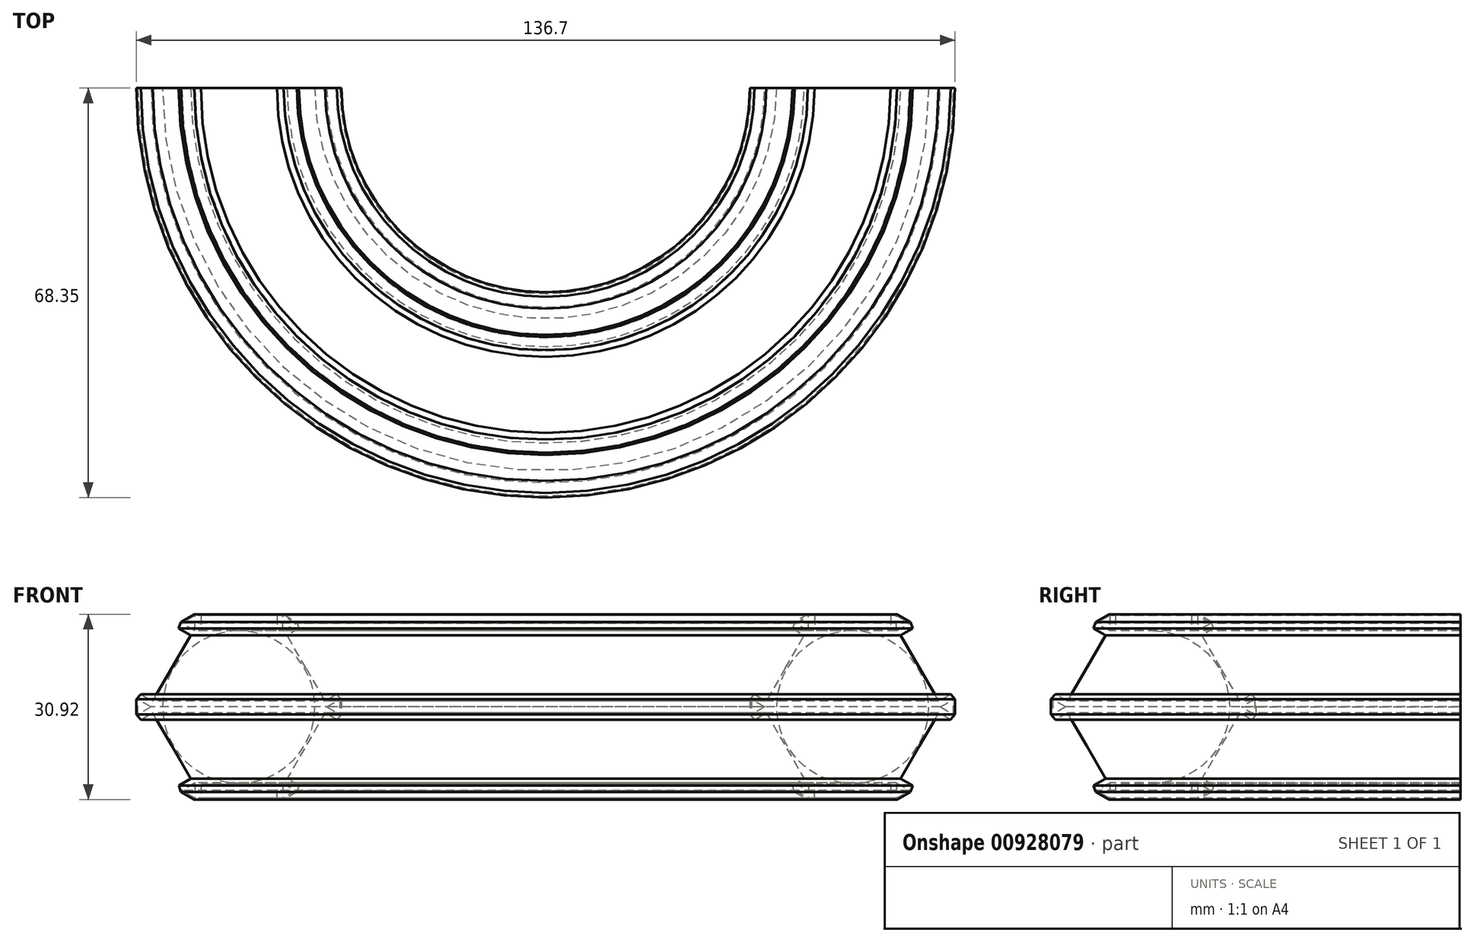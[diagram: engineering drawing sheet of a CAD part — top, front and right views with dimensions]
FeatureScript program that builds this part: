
annotation { "Feature Type Name" : "Feature", "Feature Type Description" : "" }
export const myFeature = defineFeature(function(context is Context, id is Id, definition is map)
    precondition{}
    {
        {
            var Q0;
            Q0=qCreatedBy(makeId("Top.planeOp"),FACE);
            var sketch = newSketch(context, id + "F0", { "sketchPlane" : qUnion([Q0])});
            skLineSegment(sketch, "E0", {"start": v(0, 0) * mm, "end": v(-50.8, 0) * mm});
            skCircle(sketch, "E1", {"center": v(0, 0) * mm, "radius": 50.8 * mm});
            skSolve(sketch);
        }
        {
            var Q0;
            Q0=qCreatedBy(makeId("Front.planeOp"),FACE);
            var sketch = newSketch(context, id + "F1", { "sketchPlane" : qUnion([Q0])});
            skCircle(sketch, "E2", {"center": v(-51.22, 0) * mm, "radius": 12.7 * mm});
            skPoint(sketch, "E3.0.midPoint", {"position": v(-51.22, 12.7) * mm});
            skLineSegment(sketch, "E4", {"start": v(-65.88, 0) * mm, "end": v(-68.08, -1.27) * mm});
            skLineSegment(sketch, "E5", {"start": v(-58.55, -12.7) * mm, "end": v(-60.75, -13.97) * mm});
            skLineSegment(sketch, "E6", {"start": v(-58.55, -12.7) * mm, "end": v(-58.55, -15.23) * mm});
            skLineSegment(sketch, "E7", {"start": v(-43.88, -12.7) * mm, "end": v(-43.88, -15.23) * mm});
            skLineSegment(sketch, "E8", {"start": v(-43.88, -12.7) * mm, "end": v(-41.67, -13.98) * mm});
            skLineSegment(sketch, "E9", {"start": v(-36.55, 0) * mm, "end": v(-34.36, -1.26) * mm});
            skLineSegment(sketch, "E10", {"start": v(-36.55, 0) * mm, "end": v(-34.36, 1.26) * mm});
            skLineSegment(sketch, "E11", {"start": v(-43.88, 12.7) * mm, "end": v(-41.7, 13.97) * mm});
            skLineSegment(sketch, "E12", {"start": v(-58.55, 12.7) * mm, "end": v(-58.55, 15.25) * mm});
            skLineSegment(sketch, "E13", {"start": v(-43.88, 12.7) * mm, "end": v(-43.88, 15.25) * mm});
            skLineSegment(sketch, "E14", {"start": v(-58.55, 12.7) * mm, "end": v(-60.76, 13.98) * mm});
            skLineSegment(sketch, "E15", {"start": v(-65.88, 0) * mm, "end": v(-68.08, 1.27) * mm});
            skLineSegment(sketch, "E16", {"start": v(-51.22, 12.96) * mm, "end": v(-57.56, 12.96) * mm});
            skLineSegment(sketch, "E17", {"start": v(-51.22, 12.96) * mm, "end": v(-44.86, 12.96) * mm});
            skLineSegment(sketch, "E18", {"start": v(-62.43, 6.47) * mm, "end": v(-59.25, 11.97) * mm});
            skLineSegment(sketch, "E19", {"start": v(-62.43, -6.47) * mm, "end": v(-65.6, -0.98) * mm});
            skLineSegment(sketch, "E20", {"start": v(-62.43, -6.47) * mm, "end": v(-59.26, -11.97) * mm});
            skLineSegment(sketch, "E21", {"start": v(-51.22, -12.95) * mm, "end": v(-57.56, -12.95) * mm});
            skLineSegment(sketch, "E22", {"start": v(-51.22, -12.95) * mm, "end": v(-44.86, -12.95) * mm});
            skLineSegment(sketch, "E23", {"start": v(-40, -6.48) * mm, "end": v(-36.83, -0.97) * mm});
            skLineSegment(sketch, "E24", {"start": v(-40, -6.48) * mm, "end": v(-43.16, -11.98) * mm});
            skLineSegment(sketch, "E25", {"start": v(-40, 6.48) * mm, "end": v(-43.17, 11.98) * mm});
            skLineSegment(sketch, "E26", {"start": v(-40, 6.48) * mm, "end": v(-36.83, 1) * mm});
            skLineSegment(sketch, "E27", {"start": v(-62.43, 6.47) * mm, "end": v(-65.6, 0.96) * mm});
            skLineSegment(sketch, "E28", {"start": v(-61.25, 13.12) * mm, "end": v(-59.25, 11.97) * mm});
            skLineSegment(sketch, "E29", {"start": v(-57.56, 15.25) * mm, "end": v(-57.56, 12.96) * mm});
            skLineSegment(sketch, "E30", {"start": v(-67.6, -2.12) * mm, "end": v(-65.6, -0.98) * mm});
            skLineSegment(sketch, "E31", {"start": v(-44.86, -15.23) * mm, "end": v(-44.86, -12.95) * mm});
            skLineSegment(sketch, "E32", {"start": v(-57.56, -12.95) * mm, "end": v(-57.56, -15.23) * mm});
            skLineSegment(sketch, "E33", {"start": v(-41.18, -13.12) * mm, "end": v(-43.16, -11.98) * mm});
            skLineSegment(sketch, "E34", {"start": v(-34.85, -2.11) * mm, "end": v(-36.83, -0.97) * mm});
            skLineSegment(sketch, "E35", {"start": v(-34.86, 2.13) * mm, "end": v(-36.83, 1) * mm});
            skLineSegment(sketch, "E36", {"start": v(-41.2, 13.11) * mm, "end": v(-43.17, 11.98) * mm});
            skLineSegment(sketch, "E37", {"start": v(-44.86, 15.25) * mm, "end": v(-44.86, 12.96) * mm});
            skLineSegment(sketch, "E38", {"start": v(-61.24, -13.11) * mm, "end": v(-59.26, -11.97) * mm});
            skLineSegment(sketch, "E39", {"start": v(-67.6, 2.11) * mm, "end": v(-65.6, 0.96) * mm});
            skLineSegment(sketch, "E40", {"start": v(-51.22, 12.7) * mm, "end": v(-51.22, 0) * mm});
            skLineSegment(sketch, "E41", {"start": v(-34.36, 1.26) * mm, "end": v(-34.36, -1.26) * mm});
            skLineSegment(sketch, "E42", {"start": v(-41.67, -13.98) * mm, "end": v(-43.88, -15.23) * mm});
            skLineSegment(sketch, "E43", {"start": v(-58.55, -15.23) * mm, "end": v(-60.75, -13.97) * mm});
            skLineSegment(sketch, "E44", {"start": v(-68.08, -1.27) * mm, "end": v(-68.08, 1.27) * mm});
            skLineSegment(sketch, "E45", {"start": v(-58.55, 15.25) * mm, "end": v(-60.76, 13.98) * mm});
            skLineSegment(sketch, "E46", {"start": v(-58.68, 15.48) * mm, "end": v(-57.56, 15.25) * mm});
            skLineSegment(sketch, "E47", {"start": v(-58.68, 15.48) * mm, "end": v(-60.89, 14.2) * mm});
            skLineSegment(sketch, "E48", {"start": v(-60.89, 14.2) * mm, "end": v(-61.25, 13.12) * mm});
            skLineSegment(sketch, "E49", {"start": v(-68.35, -1.27) * mm, "end": v(-67.6, -2.12) * mm});
            skLineSegment(sketch, "E50", {"start": v(-68.35, -1.27) * mm, "end": v(-68.35, 1.27) * mm});
            skLineSegment(sketch, "E51", {"start": v(-68.35, 1.27) * mm, "end": v(-67.6, 2.11) * mm});
            skLineSegment(sketch, "E52", {"start": v(-41.7, 13.97) * mm, "end": v(-43.88, 15.25) * mm});
            skLineSegment(sketch, "E53", {"start": v(-43.76, 15.47) * mm, "end": v(-44.86, 15.25) * mm});
            skLineSegment(sketch, "E54", {"start": v(-41.56, 14.2) * mm, "end": v(-41.2, 13.11) * mm});
            skLineSegment(sketch, "E55", {"start": v(-43.76, 15.47) * mm, "end": v(-41.56, 14.2) * mm});
            skLineSegment(sketch, "E56", {"start": v(-58.67, -15.44) * mm, "end": v(-57.56, -15.23) * mm});
            skLineSegment(sketch, "E57", {"start": v(-60.88, -14.2) * mm, "end": v(-61.24, -13.11) * mm});
            skLineSegment(sketch, "E58", {"start": v(-60.88, -14.2) * mm, "end": v(-58.67, -15.44) * mm});
            skLineSegment(sketch, "E59", {"start": v(-43.76, -15.44) * mm, "end": v(-44.86, -15.23) * mm});
            skLineSegment(sketch, "E60", {"start": v(-41.54, -14.2) * mm, "end": v(-41.18, -13.12) * mm});
            skLineSegment(sketch, "E61", {"start": v(-41.54, -14.2) * mm, "end": v(-43.76, -15.44) * mm});
            skLineSegment(sketch, "E62", {"start": v(-34.1, -1.26) * mm, "end": v(-34.85, -2.11) * mm});
            skLineSegment(sketch, "E63", {"start": v(-34.1, 1.26) * mm, "end": v(-34.86, 2.13) * mm});
            skLineSegment(sketch, "E64", {"start": v(-34.1, 1.26) * mm, "end": v(-34.1, -1.26) * mm});
            skSolve(sketch);
        }
        {
            var Q0;
            Q0=makeQuery(id+"F1.imprint","IMPRINT",FACE,{"disambiguationData":[TD([[makeQuery(id+"F1.imprint","IMPRINT",EDGE,{"derivedFrom":sQuery(id+"F1.wireOp",EDGE,"E2")}),-1.0]])]});
            var Q1;
            Q1=sQuery(id+"F0.wireOp",EDGE,"E1");
            revolve(context, id + "F2", {"surfaceOperationType" : NewSurfaceOperationType.NEW, "entities" : qUnion([Q0]), "axis" : qUnion([Q1]), "revolveType" : RevolveType.ONE_DIRECTION, "angle" : 180 * degree});
        }
    });
